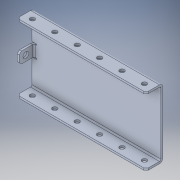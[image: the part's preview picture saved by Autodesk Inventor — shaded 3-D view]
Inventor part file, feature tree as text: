
AUTODESK INVENTOR PART (.ipt)
format: ipt  version: 2017.1 (Build 211199000, 199)  size: 159,744 bytes
history: native  units: in
note: dims shown in document units (in); Inventor stores cm internally (conversion verified against a paired STEP export)
features: chamfer x1
ambient origin geometry x8: Origin, YZ Plane, XZ Plane, XY Plane, X Axis, Y Axis, Z Axis, Center Point
bodies: Solid1 (feature_tree)
feature tree (1):
  chamfer  "Chamfer1"  [1 undecoded]
note: 1 required parameter value undecoded (feature->parameter linkage not recoverable at this tier; creation-order binding heuristic only, values carry confidence <= 0.55)
